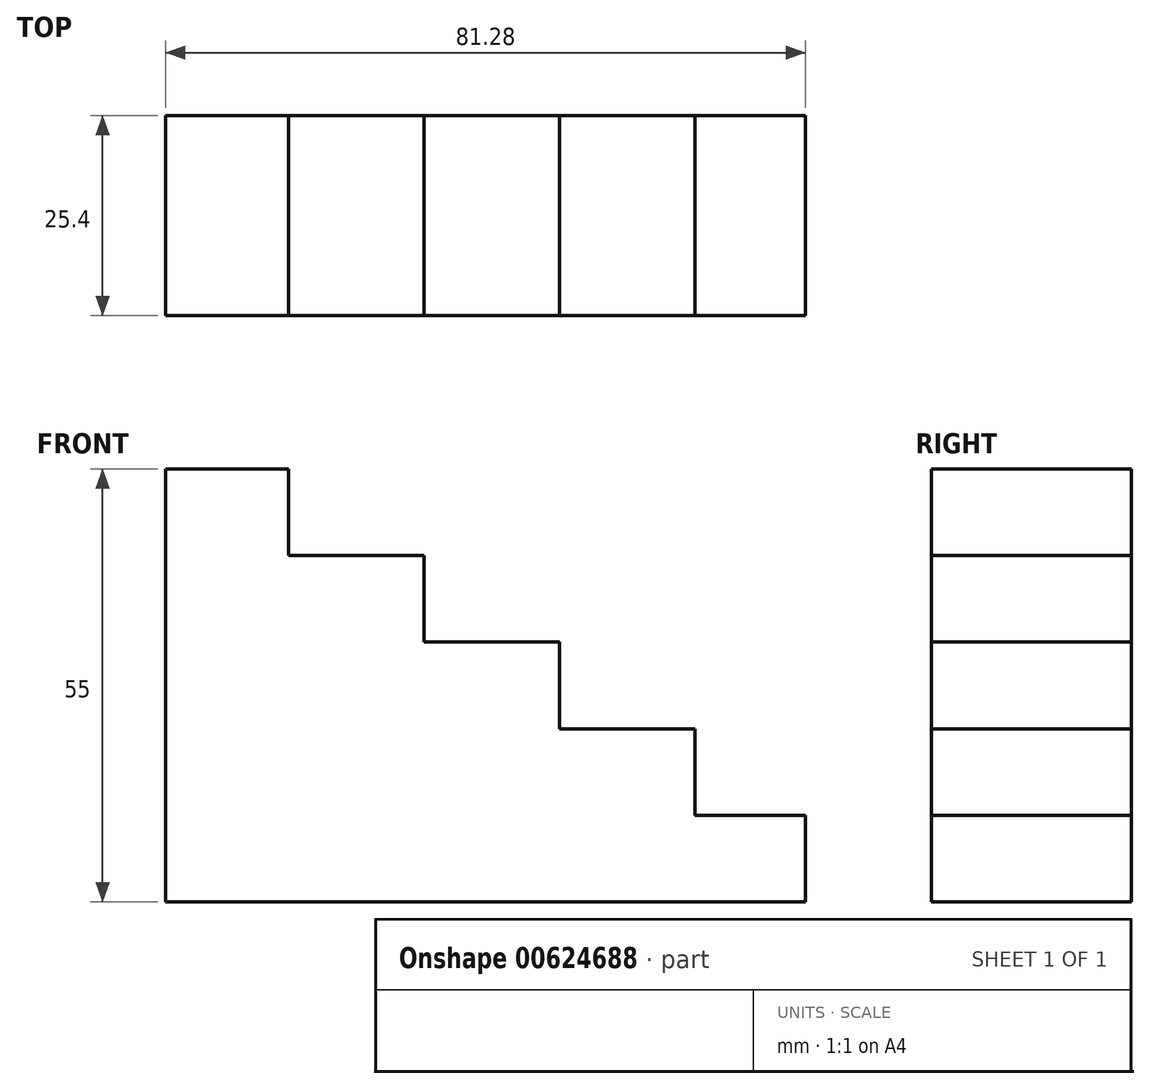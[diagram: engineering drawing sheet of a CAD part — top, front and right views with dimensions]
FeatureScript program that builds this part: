
annotation { "Feature Type Name" : "Feature", "Feature Type Description" : "" }
export const myFeature = defineFeature(function(context is Context, id is Id, definition is map)
    precondition{}
    {
        {
            var Q0;
            Q0=qCreatedBy(makeId("Front.planeOp"),FACE);
            var sketch = newSketch(context, id + "F0", { "sketchPlane" : qUnion([Q0])});
            skLineSegment(sketch, "E0.bottom", {"start": v(40.64, -5.5) * mm, "end": v(-40.64, -5.5) * mm});
            skLineSegment(sketch, "E0.top", {"start": v(40.64, 5.5) * mm, "end": v(-40.64, 5.5) * mm});
            skLineSegment(sketch, "E0.left", {"start": v(40.64, -5.5) * mm, "end": v(40.64, 5.5) * mm});
            skLineSegment(sketch, "E0.right", {"start": v(-40.64, -5.5) * mm, "end": v(-40.64, 5.5) * mm});
            skPoint(sketch, "E0.middle", {"position": v(0, 0) * mm});
            skLineSegment(sketch, "E1.bottom", {"start": v(26.6, 5.5) * mm, "end": v(9.4, 5.5) * mm});
            skLineSegment(sketch, "E1.top", {"start": v(26.6, 16.5) * mm, "end": v(9.4, 16.5) * mm});
            skLineSegment(sketch, "E1.left", {"start": v(26.6, 5.5) * mm, "end": v(26.6, 16.5) * mm});
            skLineSegment(sketch, "E1.right", {"start": v(9.4, 5.5) * mm, "end": v(9.4, 16.5) * mm});
            skLineSegment(sketch, "E2.bottom", {"start": v(9.4, 5.5) * mm, "end": v(-7.8, 5.5) * mm});
            skLineSegment(sketch, "E2.top", {"start": v(9.4, 27.5) * mm, "end": v(-7.8, 27.5) * mm});
            skLineSegment(sketch, "E2.left", {"start": v(9.4, 5.5) * mm, "end": v(9.4, 27.5) * mm});
            skLineSegment(sketch, "E2.right", {"start": v(-7.8, 5.5) * mm, "end": v(-7.8, 27.5) * mm});
            skLineSegment(sketch, "E3.bottom", {"start": v(-7.8, 5.5) * mm, "end": v(-25, 5.5) * mm});
            skLineSegment(sketch, "E3.top", {"start": v(-7.8, 38.5) * mm, "end": v(-25, 38.5) * mm});
            skLineSegment(sketch, "E3.left", {"start": v(-7.8, 5.5) * mm, "end": v(-7.8, 38.5) * mm});
            skLineSegment(sketch, "E3.right", {"start": v(-25, 5.5) * mm, "end": v(-25, 38.5) * mm});
            skLineSegment(sketch, "E4.bottom", {"start": v(-40.64, 5.5) * mm, "end": v(-25, 5.5) * mm});
            skLineSegment(sketch, "E4.top", {"start": v(-40.64, 49.5) * mm, "end": v(-25, 49.5) * mm});
            skLineSegment(sketch, "E4.left", {"start": v(-40.64, 5.5) * mm, "end": v(-40.64, 49.5) * mm});
            skLineSegment(sketch, "E4.right", {"start": v(-25, 5.5) * mm, "end": v(-25, 49.5) * mm});
            skSolve(sketch);
        }
        {
            var Q0;
            Q0 = qSketchRegion(id + "F0", true);
            extrude(context, id + "F1", {"entities" : qUnion([Q0]), "depth" : 25.4 * mm, "offsetDistance" : 25.4 * mm});
        }
    });
